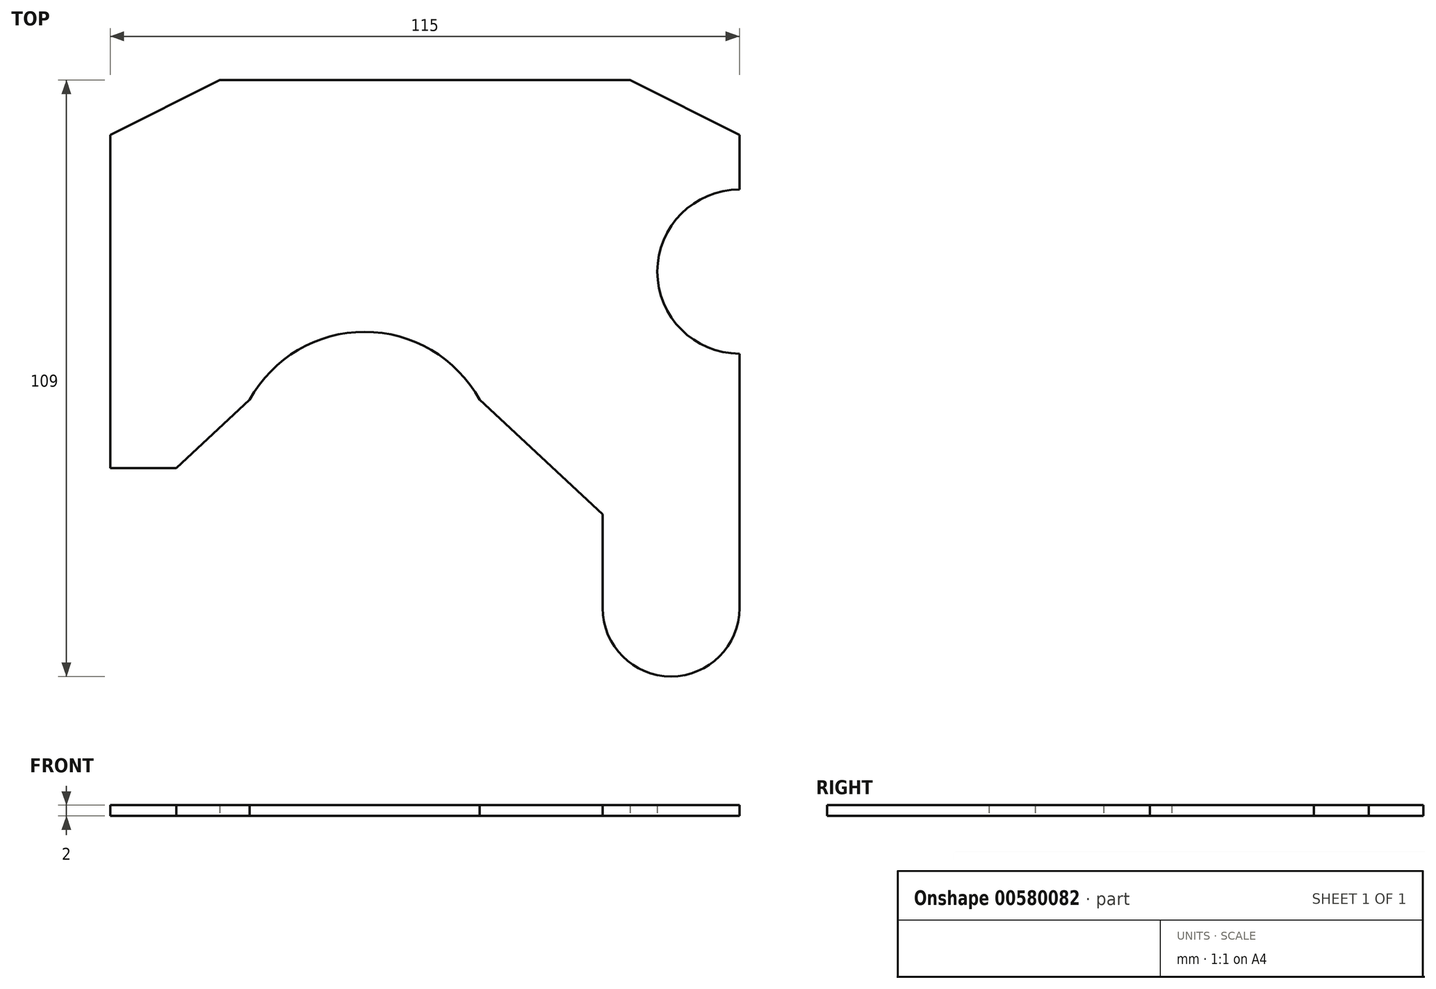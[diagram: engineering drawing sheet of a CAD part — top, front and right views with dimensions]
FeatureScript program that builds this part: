
annotation { "Feature Type Name" : "Feature", "Feature Type Description" : "" }
export const myFeature = defineFeature(function(context is Context, id is Id, definition is map)
    precondition{}
    {
        {
            var Q0;
            Q0=qCreatedBy(makeId("Top.planeOp"),FACE);
            var sketch = newSketch(context, id + "F0", { "sketchPlane" : qUnion([Q0])});
            skLineSegment(sketch, "E0.bottom", {"start": v(-48.52, 30.73) * mm, "end": v(26.48, 30.73) * mm});
            skLineSegment(sketch, "E0.left", {"start": v(-68.52, 20.73) * mm, "end": v(-68.52, -40.2) * mm});
            skLineSegment(sketch, "E0.right", {"start": v(46.48, 20.73) * mm, "end": v(46.48, 10.73) * mm});
            skLineSegment(sketch, "E1", {"start": v(21.48, -65.77) * mm, "end": v(21.48, -48.64) * mm});
            skArc(sketch, "E2", {"start": v(-1, -27.67) * mm, "mid": v(-22.02, -15.27) * mm, "end": v(-43.03, -27.67) * mm});
            skLineSegment(sketch, "E3", {"start": v(-68.52, -40.2) * mm, "end": v(-56.46, -40.2) * mm});
            skLineSegment(sketch, "E4", {"start": v(-68.52, 20.73) * mm, "end": v(-48.52, 30.73) * mm});
            skLineSegment(sketch, "E5", {"start": v(26.48, 30.73) * mm, "end": v(46.48, 20.73) * mm});
            skArc(sketch, "E6", {"start": v(46.48, 10.73) * mm, "mid": v(31.48, -4.27) * mm, "end": v(46.48, -19.27) * mm});
            skLineSegment(sketch, "E7.trimOffspring", {"start": v(46.48, -19.27) * mm, "end": v(46.48, -65.77) * mm});
            skLineSegment(sketch, "E8", {"start": v(-1, -27.67) * mm, "end": v(21.48, -48.64) * mm});
            skArc(sketch, "E9", {"start": v(21.48, -65.77) * mm, "mid": v(33.98, -78.27) * mm, "end": v(46.48, -65.77) * mm});
            skPoint(sketch, "E9.centerSnap0", {"position": v(33.98, -74.27) * mm});
            skPoint(sketch, "E9.centerSnap1", {"position": v(21.48, -65.77) * mm});
            skLineSegment(sketch, "E10", {"start": v(-43.03, -27.67) * mm, "end": v(-56.46, -40.2) * mm});
            skSolve(sketch);
        }
        {
            var Q0;
            Q0=makeQuery(id+"F0.imprint","IMPRINT",FACE,{"disambiguationData":[TD([[makeQuery(id+"F0.imprint","IMPRINT",EDGE,{"derivedFrom":sQuery(id+"F0.wireOp",EDGE,"E0.bottom")}),-1.0]])]});
            extrude(context, id + "F1", {"entities" : qUnion([Q0]), "depth" : 2 * mm, "offsetDistance" : 25 * mm});
        }
    });
